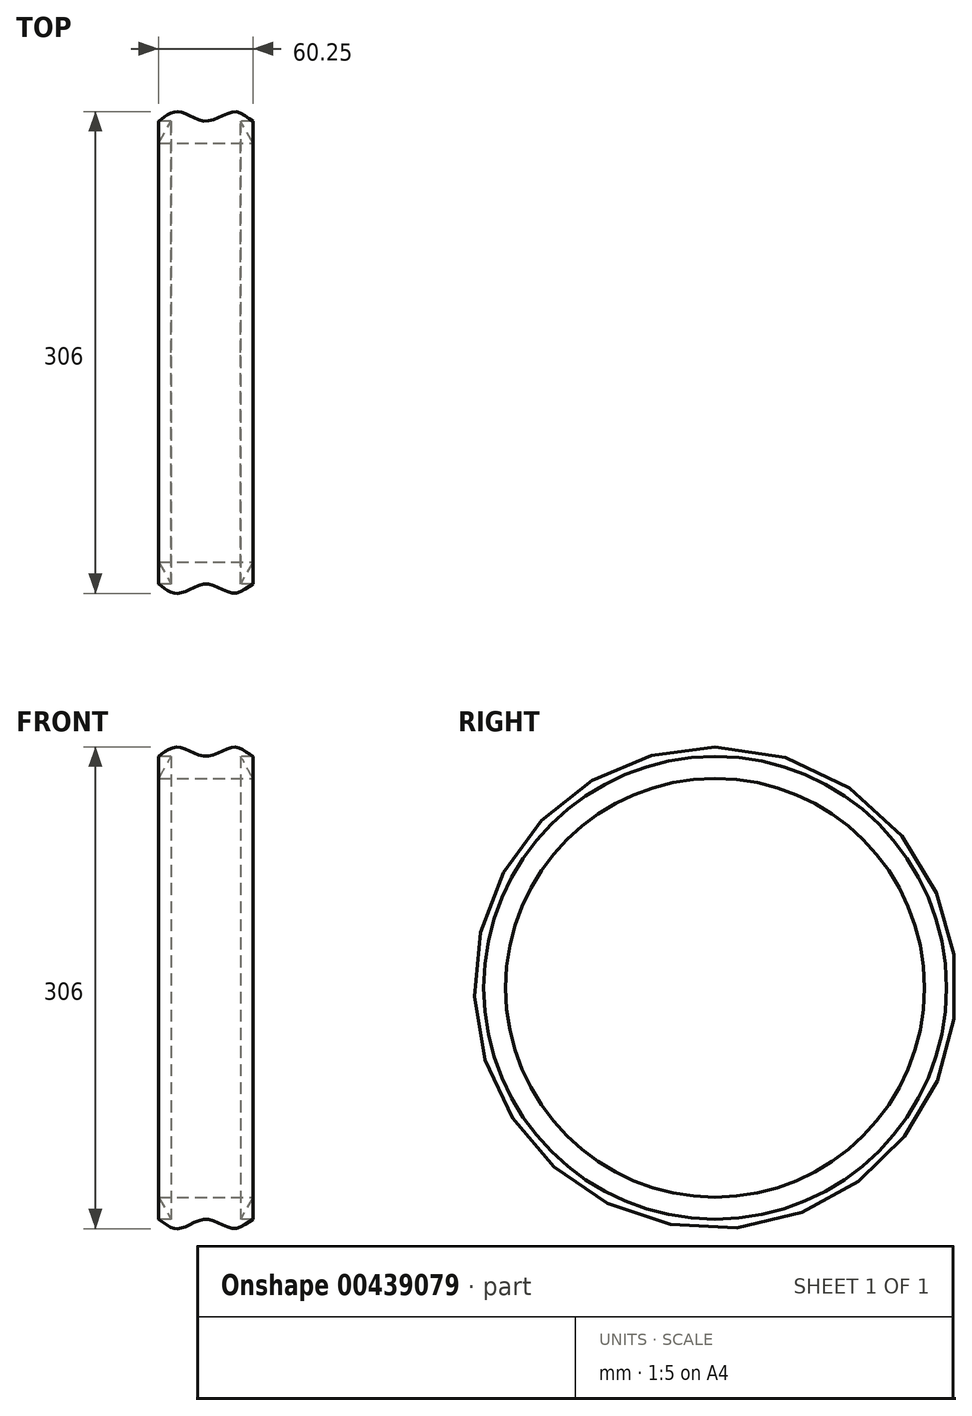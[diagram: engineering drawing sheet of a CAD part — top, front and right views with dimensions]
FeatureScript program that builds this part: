
annotation { "Feature Type Name" : "Feature", "Feature Type Description" : "" }
export const myFeature = defineFeature(function(context is Context, id is Id, definition is map)
    precondition{}
    {
        {
            var Q0;
            Q0=qCreatedBy(makeId("Front.planeOp"),FACE);
            var sketch = newSketch(context, id + "F0", { "sketchPlane" : qUnion([Q0])});
            skLineSegment(sketch, "E0.top", {"start": v(-69.43, 133) * mm, "end": v(-9.68, 133) * mm});
            skLineSegment(sketch, "E1", {"start": v(-69.43, 133) * mm, "end": v(-61.68, 147) * mm});
            skLineSegment(sketch, "E2", {"start": v(-9.68, 133) * mm, "end": v(-17.43, 147) * mm});
            skLineSegment(sketch, "E3", {"start": v(-61.68, 147) * mm, "end": v(-69.68, 147) * mm});
            skLineSegment(sketch, "E4", {"start": v(-17.43, 147) * mm, "end": v(-9.43, 147) * mm});
            skPoint(sketch, "E5.2.internal.snap0", {"position": v(-39.43, 153) * mm});
            skFitSpline(sketch, "E5", {"points": [v(-69.68, 147) * mm, v(-57.43, 153) * mm, v(-39.43, 147) * mm, v(-21.43, 153) * mm, v(-9.43, 147) * mm], "startDerivative": vector(43.1, 28.99) * mm, "endDerivative": vector(58.89, -27.2) * mm});
            skLineSegment(sketch, "E6.bottom", {"start": v(-69.43, 133) * mm, "end": v(-9.43, 133) * mm});
            skLineSegment(sketch, "E6.top", {"start": v(-69.43, 0) * mm, "end": v(-9.43, 0) * mm});
            skLineSegment(sketch, "E6.left", {"start": v(-69.43, 133) * mm, "end": v(-69.43, 0) * mm});
            skLineSegment(sketch, "E6.right", {"start": v(-9.43, 133) * mm, "end": v(-9.43, 0) * mm});
            skSolve(sketch);
        }
        {
            var Q0;
            Q0 = qSketchRegion(id + "F0", true);
            var Q1;
            Q1=sQuery(id+"F0.wireOp",EDGE,"E6.top");
            revolve(context, id + "F1", {"entities" : qUnion([Q0]), "axis" : qUnion([Q1]), "revolveType" : RevolveType.FULL});
        }
        {
            var Q0;
            Q0=makeQuery(id+"F1.opRevolve","SWEPT_FACE",FACE,{"disambiguationData":[OSD([sQuery(id+"F0.wireOp",EDGE,"E6.right")])]});
            var sketch = newSketch(context, id + "F2", { "sketchPlane" : qUnion([Q0])});
            skCircle(sketch, "E7", {"center": v(0, 0) * mm, "radius": 133 * mm});
            skSolve(sketch);
        }
        {
            var Q0;
            Q0 = qSketchRegion(id + "F2", true);
            extrude(context, id + "F3", {"entities" : qUnion([Q0]), "operationType" : NewBodyOperationType.REMOVE, "oppositeDirection" : true, "depth" : 60 * mm});
        }
    });
